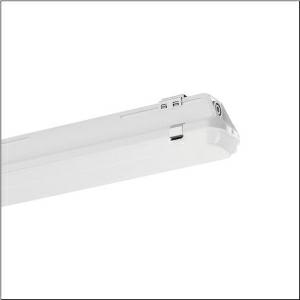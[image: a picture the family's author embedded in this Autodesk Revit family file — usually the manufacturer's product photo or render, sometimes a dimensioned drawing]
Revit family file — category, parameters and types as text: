
# Revit family: monsun_r__21_51fb107p440j_37a7
name_source: partatom
category: Lighting Fixtures
units: mm (PartAtom-declared; Revit-internal decimal feet)

## family parameters
Cut with Voids When Loaded = No
Host = Face
Light Source = No
Part Type = Normal
Room Calculation Point = No
Round Connector Dimension = Use Diameter
Shared = No

## types (1)
- Monsun® 21 (1 x LED, 4560 lm, 28.2 W, 4000K)
    Apparent Load = 28 VA
    CIE Flux Codes = 47 77 93 94 100
    Color Rendering = 80
    Color Temperature = 4000K
    Default Elevation = 1800 mm
    Description = Monsun® 21, damp-proof luminaire, chain hanger, primary optical cover: enclosure, of PMMA, light emission: direct distribution, primary light characteristic: symmetric, installation type: suspended mounting, surface-mounted, horizontal mounting, vertical mounting, LED, rated luminous flux: 4.360lm, luminous efficacy: 161lm/W, light colour: 840, colour temperature: 4000K, control gear: ECG, with terminal, 3-pole, max. 2.5mm², mains connection: 220..240V, AC, 50/60Hz, rated input power: 28W, housing, of glass-fibre reinforced polyester, uncoated, bright grey, length: 1.590mm, width: 90mm, height: 88mm, clip for enclosure, of stainless steel (V2A), ceiling mounting element, of stainless steel (V2A), chain hanger, of stainless steel (V2A), protection rating (complete): IP66, insulation class (complete): insulation class I (protective earthing), certification: CE, ENEC, VDE, UKCA, protection symbol: D, impact resistance: IK04, permissible operating ambient temperature: -25..+35°C, standard: EN 50419, EN 60598-2-1, corresponds to IFS (International Featured Standards) requirements for safety and quality in the food industry, for indoor or canopied outdoor use, no direct snow, no direct sun, no direct rain, packaging unit: 1 piece
    Height = 89 mm
    Lamp = 1 x LED
    Lamp Light Flux = 4560 lm
    Lamp Power = 28.2 W
    Lamp count = 1
    Length = 1590 mm
    Luminous efficacy = 162 lm/W
    Manufacturer = Siteco
    ModVariant = No
    Model = 51FB107P440J
    Mounting Place = Ceiling
    Mounting Type = Pendant
    Number of Poles = 1
    OnlyDefault = Yes
    Power Factor = 1
    Product Name = Monsun® 21
    Product group = damp-proof luminaire | ceiling pendant
    ProductGroupID = 908
    Protection Class = Protection class I
    Protection Degree = IP 66
    RLX_Detail_Level = 1
    RlxData = <blob elided: 88069 chars, md5=c6a2d1e2>
    Socket = socket
    Standby Power = 0 W
    System Light Flux = 4560 lm
    System Power = 28 W
    Type Comments = Product without accessories
    Type Image = l_1006717.jpg
    URL = http://relux.com
    VarID = ---
    Voltage = 0 V
    Weight = 0.00 kg
    Width = 90 mm

## geometry (parser evidence)
native form markers: Blend x4, Sweep x15
no freeform markers — native parametric forms only
